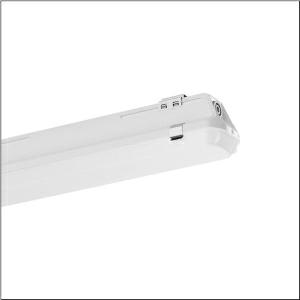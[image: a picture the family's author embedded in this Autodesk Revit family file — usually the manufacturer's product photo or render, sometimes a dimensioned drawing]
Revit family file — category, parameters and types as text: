
# Revit family: monsun_r__11_51fp22mp4b0q_0e64
name_source: partatom
category: Lighting Fixtures
units: mm (PartAtom-declared; Revit-internal decimal feet)

## family parameters
Cut with Voids When Loaded = No
Host = Face
Light Source = No
Part Type = Normal
Room Calculation Point = No
Round Connector Dimension = Use Diameter
Shared = No

## types (1)
- --- (1 x LED, 10520 lm, 66.2 W, 4000K)
    Apparent Load = 66 VA
    CIE Flux Codes = 49 78 94 96 100
    Color Rendering = 80
    Color Temperature = 4000K
    Default Elevation = 1800 mm
    Description = Monsun® 11, damp-proof luminaire, chain hanger, primary light control with lens, primary optical cover: enclosure, of PC, light emission: direct distribution, primary light characteristic: symmetric, installation type: suspended mounting, surface-mounted, horizontal mounting, vertical mounting, LED, rated luminous flux: 10.520lm, luminous efficacy: 159lm/W, light colour: 840, colour temperature: 4000K, control gear: ECG, with terminal, 3-pole, max. 2.5mm², mains connection: 220..240V, AC, 50/60Hz, rated input power: 66W, luminaire housing, of glass-fibre reinforced polyester, uncoated, bright grey, incl. chain hanger, length: 1.590mm, width: 90mm, height: 88mm, clip for enclosure, of stainless steel (V2A), ceiling mounting element, of stainless steel (V2A), chain hanger, of stainless steel (V2A), protection rating (complete): IP66, insulation class (complete): insulation class I (protective earthing), certification: CE, ENEC, VDE, UKCA, protection symbol: D, impact resistance: IK08, permissible operating ambient temperature: -35..+35°C, standard: EN 50419, EN 60598-2-1, no direct snow, no direct sun, no direct rain, for indoor or canopied outdoor use, corresponds to IFS (International Featured Standards) requirements for safety and quality in the food industry, contact your sales advisor before using the luminaires in applications with unclear chemical exposure, large temperature fluctuations or condensation-forming humidity, LABS conformity tested according to VDMA 24364:2018-05, packaging unit: 1 piece
    Height = 89 mm
    Lamp = 1 x LED
    Lamp Light Flux = 10520 lm
    Lamp Power = 66.2 W
    Lamp count = 1
    Length = 1590 mm
    Luminous efficacy = 159 lm/W
    Manufacturer = Siteco
    ModVariant = No
    Model = 51FP22MP4B0Q
    Mounting Place = Ceiling
    Mounting Type = Surface mounted
    Number of Poles = 1
    OnlyDefault = Yes
    Power Factor = 1
    Product Name = Monsun® 11
    Product group = damp-proof luminaire
    ProductGroupID = 301
    Protection Class = Protection class I
    Protection Degree = IP 66
    RLX_Detail_Level = 1
    RLX_Emergency_Light_Flux = 0 lm
    RLX_Emergency_Type = 0
    RLX_Emergency_Type_DB = No
    RlxData = <blob elided: 89997 chars, md5=cf2a110c>
    Socket = socket
    Standby Power = 0 W
    System Light Flux = 10520 lm
    System Power = 66 W
    Type Comments = factory setting: luminous flux: 100 % | (A | C | E) | 155 mA
    Type Image = l_1004748.jpg
    URL = http://relux.com
    VarID = @adj_156591
    Voltage = 0 V
    Weight = 0.00 kg
    Width = 90 mm

## geometry (parser evidence)
native form markers: Blend x4, Sweep x12
no freeform markers — native parametric forms only
